# Revit family: Wood_Lockers-Salsbury_Industries-31000_Series-3_Wide_Units
name_source: partatom
category: Specialty Equipment
units: mm (PartAtom-declared; Revit-internal decimal feet)

## family parameters
Always vertical = Yes
Classification Number = 23.40.00.00
Cut with Voids When Loaded = No
Enable Cutting in Views = No
Maintain Annotation Orientation = No
Part Type = Normal
Room Calculation Point = No
Round Connector Dimension = Use Diameter
Shared = No
Work Plane-Based = No

## types (12) — shared parameters
Assembly Code = C1030310
Building Codes = https://www.lockers.com
Construction Details = https://www.lockers.com
Default Elevation = 0.000"
Green Building-LEED = https://www.arcat.com
Hardware = Aluminum - Salsbury Finish - Black Satin
Installation-Fabrication = https://www.lockers.com
Keynote = 10 51 00
Manufacturer = Salsbury Industries
Manufacturer Fax = 1-800-562-5399
Manufacturer Website = https://www.lockers.com
MasterFormat Code = 10 51 23
MasterFormat Title = Lockers
OmniClass 23 Number = 23.40.00.00
OmniClass 23 Title = Equipment and Furnishings
Primary Structure Materials = Particle Board Industrial Grade - Salsbury Finish - White Melamine Inlay
Product Data = https://www.lockers.com
Revision = R1_2018-10
Sales Information = https://www.lockers.com
Secondary Structure Materials = Particle Board Industrial Grade - Salsbury Finish - Black Melamine Overlay
Specification = https://www.lockers.com
Test Data = https://www.lockers.com
Type Comments = Designer Wood Lockers - Single Tier
URL = www.lockers.com
Unit Trim = Melamine - Salsbury Finish - Black
Width = 36.000"

## per-type parameters (varying)
| type | Base | Base Height | Depth | Description | Door Location D1 | Model | Sloping Hood Height | Unit Height | Version |
| 31365 | Wood Locker Bases : Base - 36" W x 15" D Lockers | 4.000" | 15.000" | 3 Wide - 6 Feet High - 15 inches Deep - with Base | Wood Locker Doors : Single Tier Door for Six Foot High Locker | 31365 | 5.743" | 72.000" | 2.0 (06/30/17) |
| 31365 - without Base | Wood Locker Bases : None | 0.000" | 15.000" | 3 Wide - 6 Feet High - 15 inches Deep - without Base | Wood Locker Doors : Single Tier Door for Six Foot High Locker | 31365 without Base | 5.743" | 72.000" | 2.0  (06/30/17) |
| 31368 | Wood Locker Bases : Base - 36" W x 18" D Lockers | 4.000" | 18.000" | 3 Wide - 6 Feet High - 18 inches Deep - with Base | Wood Locker Doors : Single Tier Door for Six Foot High Locker | 31368 | 6.868" | 72.000" | 2.0 (06/30/17) |
| 31368 - without Base | Wood Locker Bases : None | 0.000" | 18.000" | 3 Wide - 6 Feet High - 18 inches Deep - without Base | Wood Locker Doors : Single Tier Door for Six Foot High Locker | 31368 without Base | 6.868" | 72.000" | 2.0 (06/30/17) |
| 31361 | Wood Locker Bases : Base - 36" W x 21" D Lockers | 4.000" | 21.000" | 3 Wide - 6 Feet High - 21 inches Deep - with Base | Wood Locker Doors : Single Tier Door for Six Foot High Locker | 31361 | 7.993" | 72.000" | 2.0 (06/30/17) |
| 31361 - without Base | Wood Locker Bases : None | 0.000" | 21.000" | 3 Wide - 6 Feet High - 21 inches Deep - without Base | Wood Locker Doors : Single Tier Door for Six Foot High Locker | 31361 without Base | 7.993" | 72.000" | 2.0 (06/30/17) |
| 31355 | Wood Locker Bases : Base - 36" W x 15" D Lockers | 4.000" | 15.000" | 3 Wide - 5 Feet High - 15 inches Deep - with Base | Wood Locker Doors : Single Tier Door for Five Foot High Locker | 31355 | 5.743" | 60.000" | 2.0 (06/30/17) |
| 31355 - without Base | Wood Locker Bases : None | 0.000" | 15.000" | 3 Wide - 5 Feet High - 15 inches Deep - without Base | Wood Locker Doors : Single Tier Door for Five Foot High Locker | 31355 without Base | 5.743" | 60.000" | 2.0 (06/30/17) |
| 31358 | Wood Locker Bases : Base - 36" W x 18" D Lockers | 4.000" | 18.000" | 3 Wide - 5 Feet High - 18 inches Deep - with Base | Wood Locker Doors : Single Tier Door for Five Foot High Locker | 31358 | 6.868" | 60.000" | 2.0 (06/30/17) |
| 31358 - without Base | Wood Locker Bases : None | 0.000" | 18.000" | 3 Wide - 5 Feet High - 18 inches Deep - without Base | Wood Locker Doors : Single Tier Door for Five Foot High Locker | 31358 without Base | 6.868" | 60.000" | 2.0 (06/30/17) |
| 31351 | Wood Locker Bases : Base - 36" W x 21" D Lockers | 4.000" | 21.000" | 3 Wide - 5 Feet High - 21 inches Deep - with Base | Wood Locker Doors : Single Tier Door for Five Foot High Locker | 31351 | 7.993" | 60.000" | 2.0 (06/30/17) |
| 31351 - without Base | Wood Locker Bases : None | 0.000" | 21.000" | 3 Wide - 5 Feet High - 21 inches Deep - without Base | Wood Locker Doors : Single Tier Door for Five Foot High Locker | 31351 without Base | 7.993" | 60.000" | 2.0 (06/30/17) |

## geometry (parser evidence)
native form markers: Extrusion x1, Sweep x36
no freeform markers — native parametric forms only
